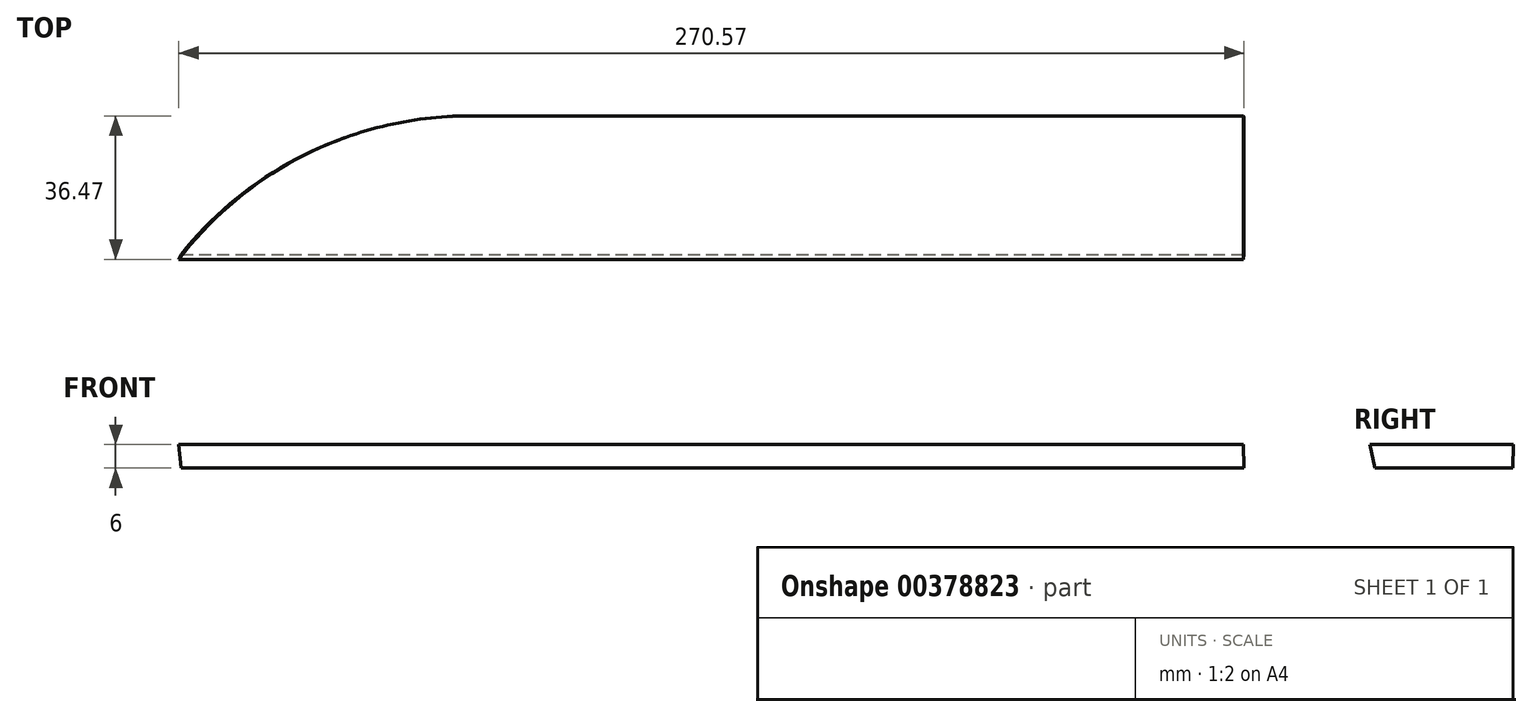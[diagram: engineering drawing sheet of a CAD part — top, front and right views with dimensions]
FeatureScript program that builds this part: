
annotation { "Feature Type Name" : "Feature", "Feature Type Description" : "" }
export const myFeature = defineFeature(function(context is Context, id is Id, definition is map)
    precondition{}
    {
        {
            var Q0;
            Q0=qCreatedBy(makeId("Top.planeOp"),FACE);
            var sketch = newSketch(context, id + "F0", { "sketchPlane" : qUnion([Q0])});
            skLineSegment(sketch, "E0.bottom", {"start": v(-69.6, 22.08) * mm, "end": v(200.4, 22.08) * mm});
            skLineSegment(sketch, "E0.top", {"start": v(-69.6, -12.92) * mm, "end": v(200.4, -12.92) * mm});
            skLineSegment(sketch, "E0.left", {"start": v(-69.6, 22.08) * mm, "end": v(-69.6, -12.92) * mm});
            skLineSegment(sketch, "E0.right", {"start": v(200.4, 22.08) * mm, "end": v(200.4, -12.92) * mm});
            skSolve(sketch);
        }
        {
            var Q0;
            Q0=makeQuery(id+"F0.imprint","IMPRINT",FACE,{"disambiguationData":[TD([[makeQuery(id+"F0.imprint","IMPRINT",EDGE,{"derivedFrom":sQuery(id+"F0.wireOp",EDGE,"E0.bottom")}),-1.0]])]});
            cPlane(context, id + "F1", {"entities" : qUnion([Q0]), "cplaneType" : CPlaneType.OFFSET, "offset" : 6 * mm, "width" : 150 * mm, "height" : 150 * mm});
        }
        {
            var Q0;
            Q0=qCreatedBy(id+"F1.planeOp",FACE);
            var sketch = newSketch(context, id + "F2", { "sketchPlane" : qUnion([Q0])});
            skLineSegment(sketch, "E1.bottom", {"start": v(-70.18, 22.26) * mm, "end": v(200.24, 22.26) * mm});
            skLineSegment(sketch, "E1.top", {"start": v(-70.18, -14.21) * mm, "end": v(200.24, -14.21) * mm});
            skLineSegment(sketch, "E1.left", {"start": v(-70.18, 22.26) * mm, "end": v(-70.18, -14.21) * mm});
            skLineSegment(sketch, "E1.right", {"start": v(200.24, 22.26) * mm, "end": v(200.24, -14.21) * mm});
            skSolve(sketch);
        }
        {
            var Q0;
            Q0=makeQuery(id+"F0.imprint","IMPRINT",FACE,{"disambiguationData":[TD([[makeQuery(id+"F0.imprint","IMPRINT",EDGE,{"derivedFrom":sQuery(id+"F0.wireOp",EDGE,"E0.bottom")}),-1.0]])]});
            var Q1;
            Q1=makeQuery(id+"F2.imprint","IMPRINT",FACE,{"disambiguationData":[TD([[makeQuery(id+"F2.imprint","IMPRINT",EDGE,{"derivedFrom":sQuery(id+"F2.wireOp",EDGE,"E1.bottom")}),-1.0]])]});
            loft(context, id + "F3", {"sheetProfilesArray" : [{ "sheetProfileEntities" : qUnion([Q0]) }, { "sheetProfileEntities" : qUnion([Q1]) }]});
        }
        {
            var Q0;
            Q0=makeQuery(id+"F3.opLoft","SWEPT_EDGE",EDGE,{"disambiguationData":[OSD([sQuery(id+"F0.wireOp",EDGE,"E0.bottom"),sQuery(id+"F0.wireOp",EDGE,"E0.left"),sQuery(id+"F2.wireOp",EDGE,"E1.bottom"),sQuery(id+"F2.wireOp",EDGE,"E1.left")])]});
            fillet(context, id + "F4", {"entities" : qUnion([Q0]), "radius" : 92.2 * mm, "tangentPropagation" : true, "allowEdgeOverflow" : false});
        }
    });
